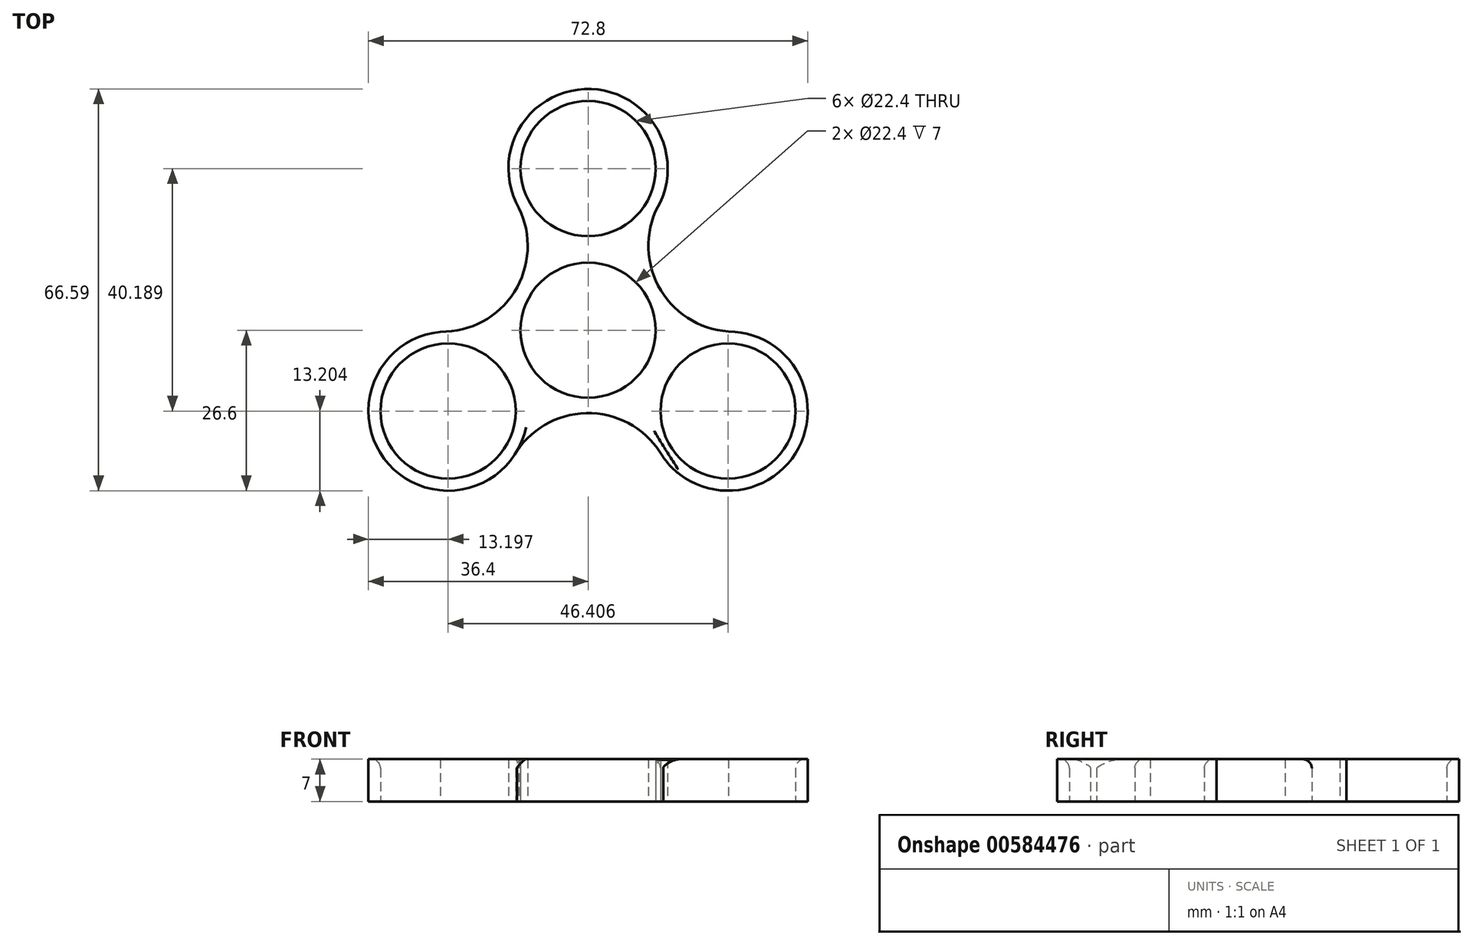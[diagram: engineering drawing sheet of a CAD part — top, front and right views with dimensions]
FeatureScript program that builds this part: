
annotation { "Feature Type Name" : "Feature", "Feature Type Description" : "" }
export const myFeature = defineFeature(function(context is Context, id is Id, definition is map)
    precondition{}
    {
        {
            var Q0;
            Q0=qCreatedBy(makeId("Top.planeOp"),FACE);
            var sketch = newSketch(context, id + "F0", { "sketchPlane" : qUnion([Q0])});
            skCircle(sketch, "E0", {"center": v(0, 0) * mm, "radius": 11.2 * mm});
            skCircle(sketch, "E1", {"center": v(0, 26.8) * mm, "radius": 11.2 * mm});
            skArc(sketch, "E2", {"start": v(11.3, 19.97) * mm, "mid": v(0.16, 40) * mm, "end": v(-11.46, 20.25) * mm});
            skCircle(sketch, "E3.1.0", {"center": v(-23.2, -13.4) * mm, "radius": 11.2 * mm});
            skArc(sketch, "E3.1.1", {"start": v(-22.95, -0.2) * mm, "mid": v(-34.71, -19.86) * mm, "end": v(-11.8, -20.05) * mm});
            skCircle(sketch, "E3.2.0", {"center": v(23.2, -13.4) * mm, "radius": 11.2 * mm});
            skArc(sketch, "E3.2.1", {"start": v(11.64, -19.77) * mm, "mid": v(34.55, -20.13) * mm, "end": v(23.26, -0.2) * mm});
            skArc(sketch, "E4", {"start": v(12, 21.31) * mm, "mid": v(11.61, 7.4) * mm, "end": v(23.26, -0.2) * mm});
            skArc(sketch, "E5.1.0", {"start": v(-24.46, -0.26) * mm, "mid": v(-12.22, 6.35) * mm, "end": v(-11.46, 20.25) * mm});
            skArc(sketch, "E5.2.0", {"start": v(12.45, -21.06) * mm, "mid": v(0.6, -13.76) * mm, "end": v(-11.8, -20.05) * mm});
            skSolve(sketch);
        }
        {
            var Q0;
            Q0=makeQuery(id+"F0.imprint","IMPRINT",FACE,{"disambiguationData":[TD([[makeQuery(id+"F0.imprint","IMPRINT",EDGE,{"derivedFrom":sQuery(id+"F0.wireOp",EDGE,"E0")}),-1.0]])]});
            extrude(context, id + "F1", {"entities" : qUnion([Q0]), "depth" : 7 * mm, "offsetDistance" : 25 * mm});
        }
        {
            var Q0;
            Q0=makeQuery(id+"F1.opExtrude","CAP_EDGE",EDGE,{"disambiguationData":[OSD([sQuery(id+"F0.wireOp",EDGE,"E5.2.0")])],"isStart":false});
            var Q1;
            Q1=makeQuery(id+"F1.opExtrude","CAP_EDGE",EDGE,{"disambiguationData":[OSD([sQuery(id+"F0.wireOp",EDGE,"E3.1.0")])],"isStart":false});
            var Q2;
            Q2=makeQuery(id+"F1.opExtrude","CAP_EDGE",EDGE,{"disambiguationData":[OSD([sQuery(id+"F0.wireOp",EDGE,"E1")])],"isStart":false});
            var Q3;
            Q3=makeQuery(id+"F1.opExtrude","CAP_EDGE",EDGE,{"disambiguationData":[OSD([sQuery(id+"F0.wireOp",EDGE,"E3.2.0")])],"isStart":false});
            fillet(context, id + "F2", {"entities" : qUnion([Q0, Q1, Q2, Q3]), "radius" : 1.5 * mm, "tangentPropagation" : true, "allowEdgeOverflow" : false});
        }
    });
